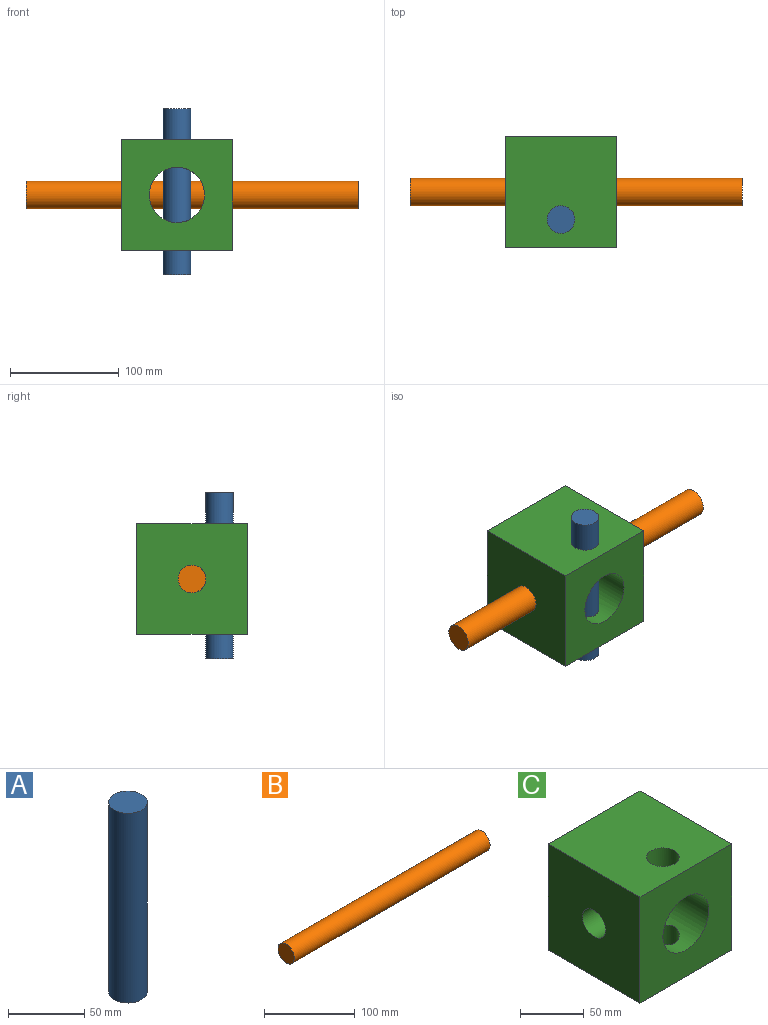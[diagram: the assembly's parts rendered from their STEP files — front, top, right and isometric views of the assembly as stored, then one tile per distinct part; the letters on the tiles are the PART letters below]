
ASSEMBLY  parts=3 mates=2
PART A: 3 faces, bbox 25.4x25.4x152.4 mm
  f0: cylinder r=12.7mm len=152.4mm, axis (0,0,-1), area 12161mm2, adj f1,f2
  f1: plane 25.4x25.4mm, normal (0,0,1), area 506.7mm2, adj f0
  f2: plane 25.4x25.4mm, normal (0,0,-1), area 506.7mm2, adj f0
PART B: 3 faces, bbox 304.8x25.4x25.4 mm
  f0: cylinder r=12.7mm len=304.8mm, axis (-1,0,0), area 24322mm2, adj f1,f2
  f1: plane 25.4x25.4mm, normal (1,0,0), area 506.7mm2, adj f0
  f2: plane 25.4x25.4mm, normal (-1,0,0), area 506.7mm2, adj f0
PART C: 11 faces, bbox 101.6x101.6x101.6 mm
  f0: plane 101.6x101.6mm, normal (0,-1,0), area 8295.7mm2, adj f1,f3,f4,f5,f6
  f1: plane 101.6x101.6mm, normal (1,0,0), area 9815.9mm2, adj f0,f2,f4,f5,f8
  f2: plane 101.6x101.6mm, normal (0,1,0), area 8295.7mm2, adj f1,f3,f4,f5,f6
  f3: plane 101.6x101.6mm, normal (-1,0,0), area 9815.9mm2, adj f0,f2,f4,f5,f7
  f4: plane 101.6x101.6mm, normal (0,0,1), area 9815.9mm2, adj f0,f1,f2,f3,f9
  f5: plane 101.6x101.6mm, normal (0,0,-1), area 9815.9mm2, adj f0,f1,f2,f3,f10
  f6: cylinder r=25.4mm len=101.6mm, axis (0,-1,0), area 14116.5mm2, adj f0,f2,f7,f8,f9,f10
  f7: cylinder r=12.7mm len=28.8mm, axis (1,0,0), area 2160.2mm2, adj f3,f6
  f8: cylinder r=12.7mm len=28.8mm, axis (1,0,0), area 2160.2mm2, adj f1,f6
  f9: cylinder r=12.7mm len=28.8mm, axis (0,0,1), area 2160.2mm2, adj f4,f6
  f10: cylinder r=12.7mm len=28.8mm, axis (0,0,1), area 2160.1mm2, adj f5,f6
PLACE A t=(0,-1.31,-124.28)mm
PLACE B t=(-189.37,-1.31,0)mm
PLACE C t=(0,-1.31,0)mm
MATE slider C.f9 <-> A.f0  axis (0,0,1) through (0,-26.71,101.6)mm
MATE slider C.f7 <-> B.f0  axis (1,0,0) through (50.8,-1.31,50.8)mm
